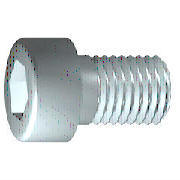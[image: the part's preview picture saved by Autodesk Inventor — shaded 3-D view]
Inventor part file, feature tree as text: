
AUTODESK INVENTOR PART (.ipt)
format: ipt  version: 2020 (Build 240168000, 168)  size: 190,976 bytes
history: native  units: mm (DEFAULTED — no unit token found)
features: sketch x2, extrude x1, plane x1, fillet x1
ambient origin geometry x7: Origin, YZ Plane, XY Plane, X Axis, Y Axis, Z Axis, Center Point
bodies: Solid1 (feature_tree), Body (feature_tree)
feature tree (5):
  extrude  "Slot"  Depth=3.5mm
  plane  "Work Plane1"
  fillet  "Fillet2"  Radius=3.5mm
  sketch  "Sketch1"  dims[d1=16.0mm d2=0.49086mm d3=3.5mm]
  sketch  "Sketch2"  dims[d4=2.7mm d5=60.0deg d6=5.0mm d7=5.0mm d8=3.464102mm d9=8.5mm d10=90.0deg d11=10.0mm d12=0.0mm d13=16.0mm d14=0.0mm d15=0.49076mm d16=0.49076mm d17=0.5mm d19=0.0mm d26=30.0mm d27=45.0deg d28=0.0mm d29=0.0mm d30=0.1mm]
